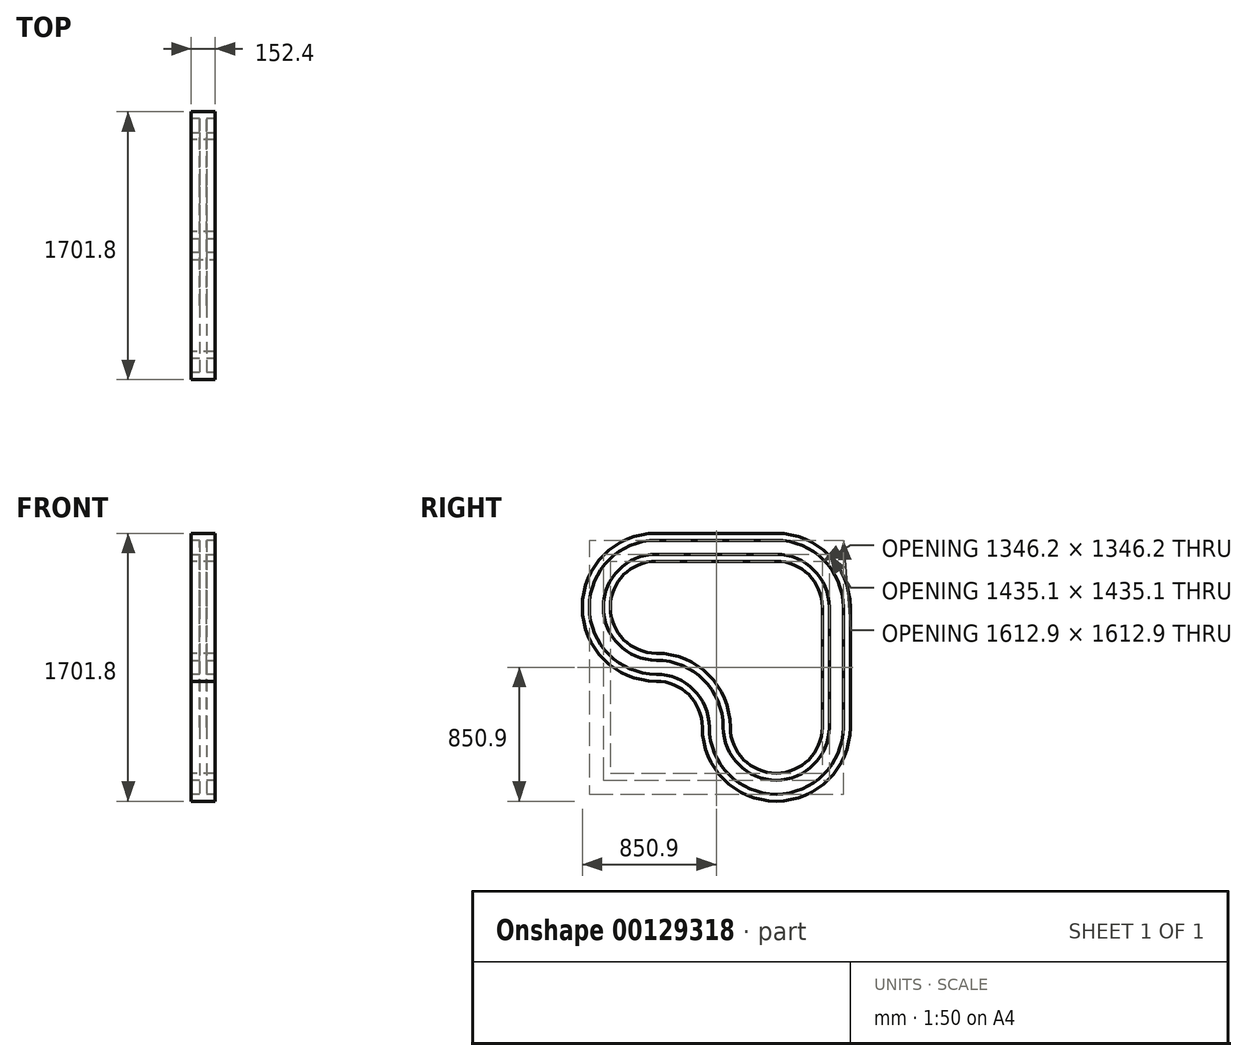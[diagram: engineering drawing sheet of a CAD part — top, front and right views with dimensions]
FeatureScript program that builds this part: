
annotation { "Feature Type Name" : "Feature", "Feature Type Description" : "" }
export const myFeature = defineFeature(function(context is Context, id is Id, definition is map)
    precondition{}
    {
        {
            var Q0;
            Q0=qCreatedBy(makeId("Front.planeOp"),FACE);
            var sketch = newSketch(context, id + "F0", { "sketchPlane" : qUnion([Q0])});
            skLineSegment(sketch, "E0", {"start": v(-76.2, 88.9) * mm, "end": v(-76.2, 44.45) * mm});
            skLineSegment(sketch, "E1", {"start": v(-76.2, 44.45) * mm, "end": v(-22.22, 44.45) * mm});
            skLineSegment(sketch, "E2", {"start": v(-22.23, 44.45) * mm, "end": v(-22.22, -44.45) * mm});
            skLineSegment(sketch, "E3", {"start": v(-22.22, -44.45) * mm, "end": v(-76.2, -44.45) * mm});
            skLineSegment(sketch, "E4", {"start": v(-76.2, -44.45) * mm, "end": v(-76.2, -88.9) * mm});
            skLineSegment(sketch, "E5", {"start": v(-76.2, -88.9) * mm, "end": v(76.2, -88.9) * mm});
            skLineSegment(sketch, "E6", {"start": v(76.2, -88.9) * mm, "end": v(76.2, -44.45) * mm});
            skLineSegment(sketch, "E7", {"start": v(76.2, -44.45) * mm, "end": v(22.22, -44.45) * mm});
            skLineSegment(sketch, "E8", {"start": v(22.22, -44.45) * mm, "end": v(22.22, 44.45) * mm});
            skLineSegment(sketch, "E9", {"start": v(22.22, 44.45) * mm, "end": v(76.2, 44.45) * mm});
            skLineSegment(sketch, "E10", {"start": v(76.2, 44.45) * mm, "end": v(76.2, 88.9) * mm});
            skLineSegment(sketch, "E11", {"start": v(76.2, 88.9) * mm, "end": v(-76.2, 88.9) * mm});
            skLineSegment(sketch, "E12", {"start": v(0, 88.9) * mm, "end": v(0, -88.9) * mm, "construction": true});
            skLineSegment(sketch, "E13", {"start": v(-22.22, 0) * mm, "end": v(22.22, 0) * mm, "construction": true});
            skSolve(sketch);
        }
        {
            var Q0;
            Q0=qCreatedBy(makeId("Right.planeOp"),FACE);
            var sketch = newSketch(context, id + "F1", { "sketchPlane" : qUnion([Q0])});
            skArc(sketch, "E14", {"start": v(381, -381) * mm, "mid": v(269.4, -111.6) * mm, "end": v(0, 0) * mm});
            skArc(sketch, "E15", {"start": v(381, -381) * mm, "mid": v(492.6, -650.4) * mm, "end": v(762, -762) * mm});
            skPoint(sketch, "E15.endSnap0", {"position": v(0, -762) * mm});
            skArc(sketch, "E16", {"start": v(762, -762) * mm, "mid": v(1031.4, -650.4) * mm, "end": v(1143, -381) * mm});
            skLineSegment(sketch, "E17", {"start": v(1143, -381) * mm, "end": v(1143, 381) * mm});
            skLineSegment(sketch, "E18", {"start": v(762, 762) * mm, "end": v(0, 762) * mm});
            skArc(sketch, "E19", {"start": v(0, 762) * mm, "mid": v(-381, 381) * mm, "end": v(0, 0) * mm});
            skPoint(sketch, "E20.visualSharp", {"position": v(1143, 762) * mm});
            skArc(sketch, "E20.filletArc", {"start": v(1143, 381) * mm, "mid": v(1031.4, 650.4) * mm, "end": v(762, 762) * mm});
            skSolve(sketch);
        }
        {
            var Q0;
            Q0=makeQuery(id+"F0.imprint","IMPRINT",FACE,{"disambiguationData":[TD([[makeQuery(id+"F0.imprint","IMPRINT",EDGE,{"derivedFrom":sQuery(id+"F0.wireOp",EDGE,"E0")}),1.0]])]});
            var Q1;
            Q1=qConstructionFilter(qBodyType(qCreatedBy(id+"F1",EDGE),BodyType.WIRE),ConstructionObject.NO);
            sweep(context, id + "F2", {"profiles" : qUnion([Q0]), "path" : qUnion([Q1])});
        }
    });
